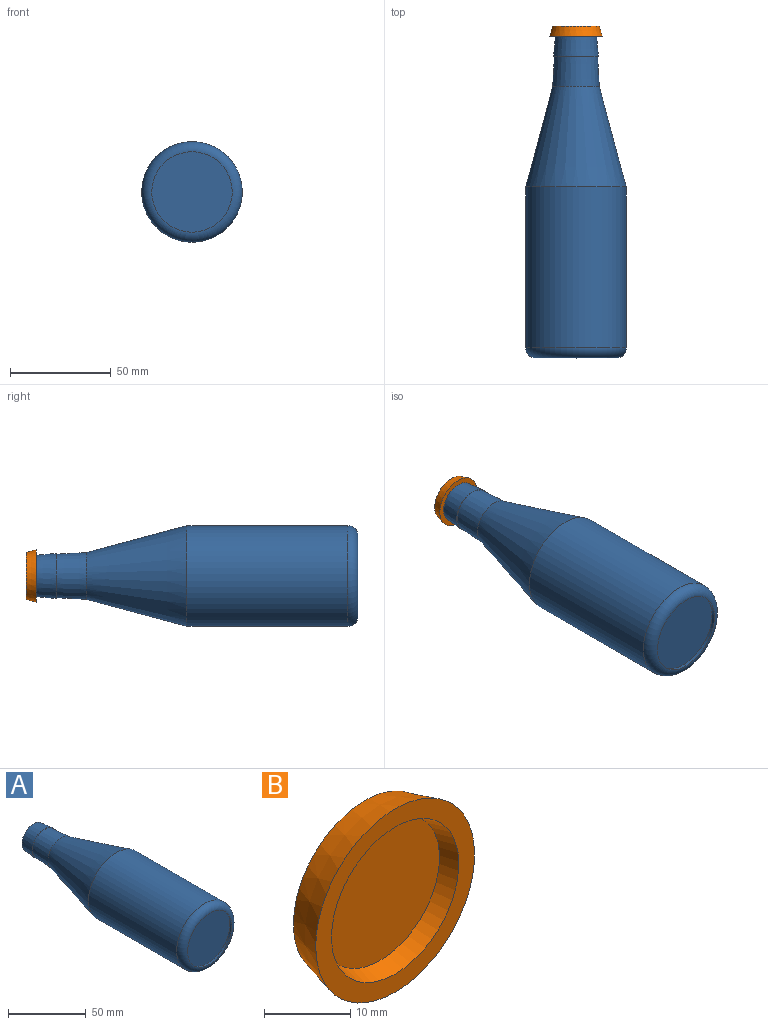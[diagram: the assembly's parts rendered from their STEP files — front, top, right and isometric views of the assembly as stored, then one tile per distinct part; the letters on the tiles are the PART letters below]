
ASSEMBLY  parts=2 mates=1
PART A: 10 faces, bbox 54.1x160x54.1 mm
  f0: cylinder r=25mm len=80mm, axis (0,1,0), area 12566.4mm2, adj f1,f4
  f1: torus R=20mm, axis (0,-1,0), area 1144mm2, adj f0,f2
  f2: cone r=20mm half-angle=10deg, axis (0,1,0), area 257.5mm2, adj f1,f3
  f3: plane 40.71x40.71mm, normal (0,-1,0), area 1301.3mm2, adj f2
  f4: cone r=25mm half-angle=15deg, axis (0,-1,0), area 5952.3mm2, adj f0,f5
  f5: cone r=11.6mm half-angle=3deg, axis (0,-1,0), area 1057.9mm2, adj f4,f7
  f6: cone r=10.29mm half-angle=5deg, axis (0,-1,0), area 676.7mm2, adj f7,f8
  f7: plane 22.33x22.33mm, normal (0,-1,0), area 24.2mm2, adj f5,f6
  f8: cylinder r=10.29mm len=125mm, axis (0,1,0), area 8083.6mm2, adj f6,f9
  f9: plane 20.58x20.58mm, normal (0,1,0), area 332.8mm2, adj f8
PART B: 5 faces, bbox 26.1x5x26.1 mm
  f0: cone r=11.69mm half-angle=15deg, axis (0,-1,0), area 401.9mm2, adj f1,f2
  f1: plane 26.05x26.05mm, normal (0,-1,0), area 190.8mm2, adj f0,f3
  f2: plane 23.37x23.37mm, normal (0,1,0), area 429.1mm2, adj f0
  f3: cone r=9.27mm half-angle=15deg, axis (0,-1,0), area 164.3mm2, adj f1,f4
  f4: plane 19.54x19.54mm, normal (0,-1,0), area 299.8mm2, adj f3
PLACE A t=(169.67,159.85,0.3)mm
PLACE B t=(260.29,274.85,-5.62)mm
MATE fastened B.f0 <-> A.f0  axis (0,-1,0) through (169.67,269.85,0.3)mm
